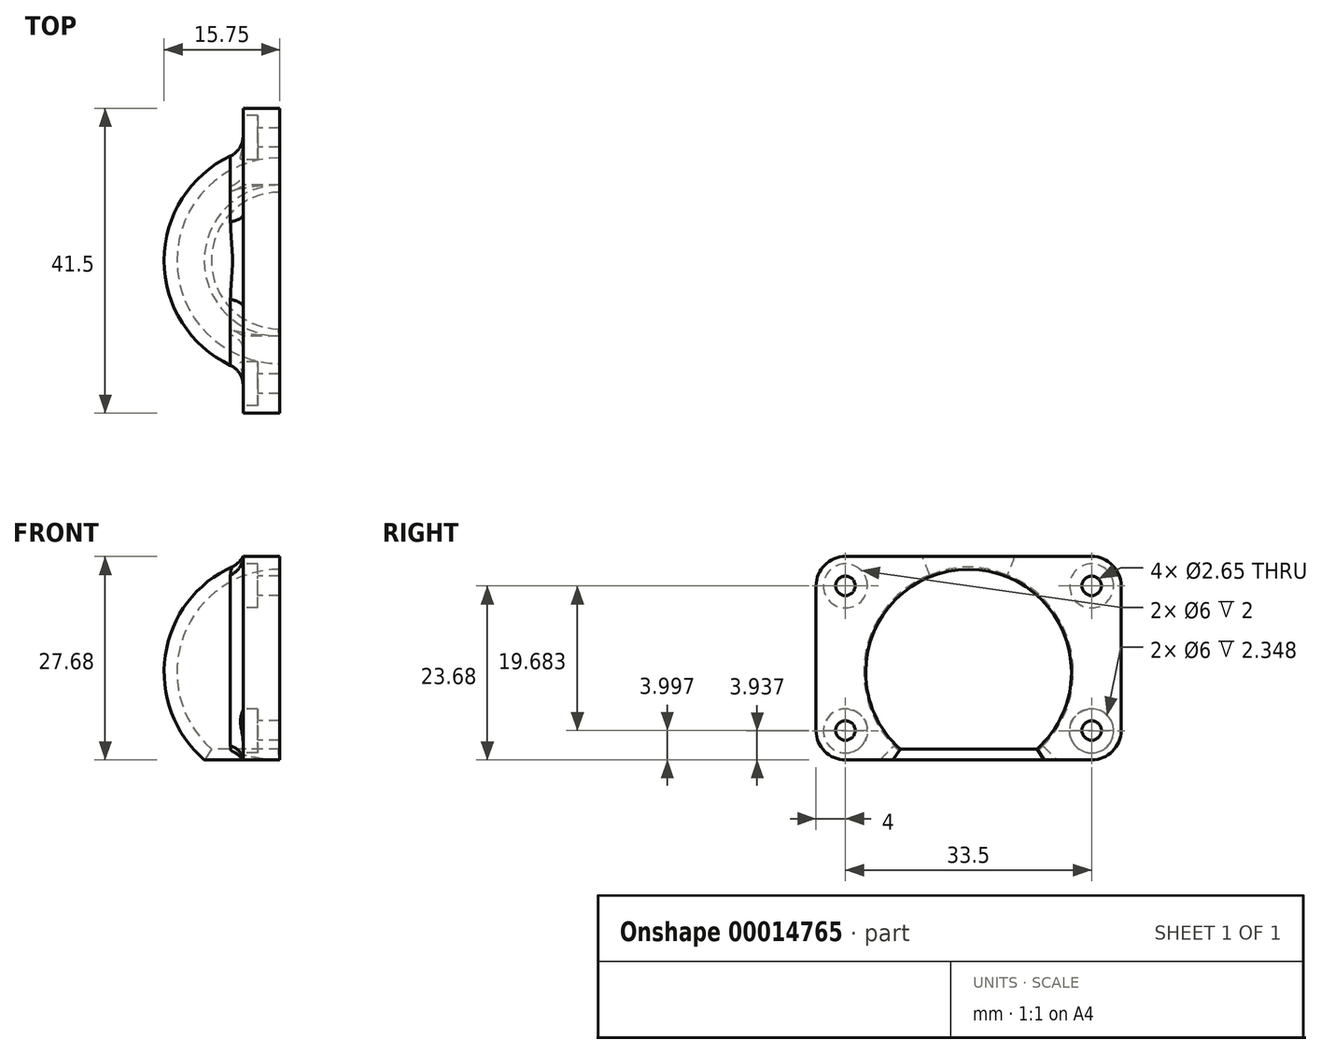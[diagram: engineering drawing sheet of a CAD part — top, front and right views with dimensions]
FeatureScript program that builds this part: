
annotation { "Feature Type Name" : "Feature", "Feature Type Description" : "" }
export const myFeature = defineFeature(function(context is Context, id is Id, definition is map)
    precondition{}
    {
        {
            var Q0;
            Q0=qCreatedBy(makeId("Top.planeOp"),FACE);
            var sketch = newSketch(context, id + "F0", { "sketchPlane" : qUnion([Q0])});
            skArc(sketch, "E0", {"start": v(0, 14) * mm, "mid": v(-14, 0) * mm, "end": v(0, -14) * mm});
            skArc(sketch, "E1", {"start": v(0, 15.75) * mm, "mid": v(-15.75, 0) * mm, "end": v(0, -15.75) * mm});
            skLineSegment(sketch, "E2", {"start": v(0, 14) * mm, "end": v(0, 15.75) * mm});
            skLineSegment(sketch, "E3", {"start": v(0, -14) * mm, "end": v(0, -15.75) * mm});
            skSolve(sketch);
        }
        {
            var Q0;
            Q0=makeQuery(id+"F0.imprint","IMPRINT",FACE,{"disambiguationData":[TD([[makeQuery(id+"F0.imprint","IMPRINT",EDGE,{"derivedFrom":sQuery(id+"F0.wireOp",EDGE,"E0")}),-1.0]])]});
            var Q1;
            Q1=sQuery(id+"F0.wireOp",EDGE,"E2");
            revolve(context, id + "F1", {"entities" : qUnion([Q0]), "axis" : qUnion([Q1]), "revolveType" : RevolveType.SYMMETRIC, "angle" : 180 * degree});
        }
        {
            var Q0;
            Q0=qCreatedBy(makeId("Top.planeOp"),FACE);
            var sketch = newSketch(context, id + "F2", { "sketchPlane" : qUnion([Q0])});
            skCircle(sketch, "E4", {"center": v(0, 0) * mm, "radius": 7.5 * mm});
            skSolve(sketch);
        }
        {
            var Q0;
            Q0=makeQuery(id+"F2.imprint","IMPRINT",FACE,{"disambiguationData":[TD([[makeQuery(id+"F2.imprint","IMPRINT",EDGE,{"derivedFrom":sQuery(id+"F2.wireOp",EDGE,"E4")}),1.0]])]});
            extrude(context, id + "F3", {"entities" : qUnion([Q0]), "operationType" : NewBodyOperationType.REMOVE, "oppositeDirection" : true, "depth" : 25 * mm});
        }
        {
            var Q0;
            Q0=qCreatedBy(makeId("Right.planeOp"),FACE);
            var sketch = newSketch(context, id + "F4", { "sketchPlane" : qUnion([Q0])});
            skPoint(sketch, "E5", {"position": v(0, -2.5) * mm});
            skLineSegment(sketch, "E6", {"start": v(2.76, -0.55) * mm, "end": v(12.1, -14.7) * mm});
            skLineSegment(sketch, "E7", {"start": v(2.76, -0.55) * mm, "end": v(0, -0.55) * mm});
            skLineSegment(sketch, "E8", {"start": v(0, -0.55) * mm, "end": v(0, -14.7) * mm});
            skLineSegment(sketch, "E9", {"start": v(0, -14.7) * mm, "end": v(12.1, -14.7) * mm});
            skPoint(sketch, "E10.left.end.orphan", {"position": v(5.75, -2.5) * mm});
            skPoint(sketch, "E11.trimOffspring.end.orphan", {"position": v(-5.75, -2.5) * mm});
            skSolve(sketch);
        }
        {
            var Q0;
            Q0=makeQuery(id+"F4.imprint","IMPRINT",FACE,{"disambiguationData":[TD([[makeQuery(id+"F4.imprint","IMPRINT",EDGE,{"derivedFrom":sQuery(id+"F4.wireOp",EDGE,"E6")}),-1.0]])]});
            var Q1;
            Q1=sQuery(id+"F4.wireOp",EDGE,"E8");
            revolve(context, id + "F5", {"operationType" : NewBodyOperationType.REMOVE, "entities" : qUnion([Q0]), "axis" : qUnion([Q1]), "revolveType" : RevolveType.FULL, "oppositeDirection" : true});
        }
        {
            var Q0;
            Q0=qCreatedBy(makeId("Right.planeOp"),FACE);
            cPlane(context, id + "F6", {"entities" : qUnion([Q0]), "cplaneType" : CPlaneType.OFFSET, "offset" : 5 * mm, "oppositeDirection" : true, "width" : 150 * mm, "height" : 150 * mm});
        }
        {
            var Q0;
            Q0=qCreatedBy(id+"F6.planeOp",FACE);
            var sketch = newSketch(context, id + "F7", { "sketchPlane" : qUnion([Q0])});
            skLineSegment(sketch, "E12.bottom", {"start": v(16.75, 15.75) * mm, "end": v(-16.75, 15.75) * mm});
            skLineSegment(sketch, "E12.top", {"start": v(16.75, -11.93) * mm, "end": v(10.28, -11.93) * mm});
            skLineSegment(sketch, "E12.left", {"start": v(20.75, 11.75) * mm, "end": v(20.75, -7.93) * mm});
            skLineSegment(sketch, "E12.right", {"start": v(-20.75, 11.75) * mm, "end": v(-20.75, -7.93) * mm});
            skPoint(sketch, "E13.visualSharp", {"position": v(-20.75, 15.75) * mm});
            skArc(sketch, "E13.filletArc", {"start": v(-16.75, 15.75) * mm, "mid": v(-19.58, 14.58) * mm, "end": v(-20.75, 11.75) * mm});
            skPoint(sketch, "E14.visualSharp", {"position": v(-20.75, -11.93) * mm});
            skArc(sketch, "E14.filletArc", {"start": v(-20.75, -7.93) * mm, "mid": v(-19.58, -10.76) * mm, "end": v(-16.75, -11.93) * mm});
            skPoint(sketch, "E15.visualSharp", {"position": v(20.75, -11.93) * mm});
            skArc(sketch, "E15.filletArc", {"start": v(16.75, -11.93) * mm, "mid": v(19.58, -10.76) * mm, "end": v(20.75, -7.93) * mm});
            skPoint(sketch, "E16.visualSharp", {"position": v(20.75, 15.75) * mm});
            skArc(sketch, "E16.filletArc", {"start": v(20.75, 11.75) * mm, "mid": v(19.58, 14.58) * mm, "end": v(16.75, 15.75) * mm});
            skArc(sketch, "E17", {"start": v(9.3, -10.46) * mm, "mid": v(0, 14) * mm, "end": v(-9.3, -10.46) * mm});
            skLineSegment(sketch, "E18", {"start": v(-9.3, -10.46) * mm, "end": v(-10.28, -11.93) * mm});
            skLineSegment(sketch, "E19", {"start": v(9.3, -10.46) * mm, "end": v(10.28, -11.93) * mm});
            skLineSegment(sketch, "E20.trimOffspring", {"start": v(-10.28, -11.93) * mm, "end": v(-16.75, -11.93) * mm});
            skSolve(sketch);
        }
        {
            var Q0;
            Q0=makeQuery(id+"F7.imprint","IMPRINT",FACE,{"disambiguationData":[TD([[makeQuery(id+"F7.imprint","IMPRINT",EDGE,{"derivedFrom":sQuery(id+"F7.wireOp",EDGE,"E12.bottom")}),1.0]])]});
            extrude(context, id + "F8", {"entities" : qUnion([Q0]), "operationType" : NewBodyOperationType.ADD, "depth" : 5 * mm});
        }
        {
            var Q0;
            Q0=makeQuery(id+"F8.boolean.opBoolean","INTERSECT",EDGE,{"derivedFrom":[makeQuery(id+"F1.opRevolve","SWEPT_FACE",FACE,{"disambiguationData":[OSD([sQuery(id+"F0.wireOp",EDGE,"E1")])]}),makeQuery(id+"F8.opExtrude","CAP_FACE",FACE,{"disambiguationData":[OSD([sQuery(id+"F7.wireOp",EDGE,"E12.bottom"),sQuery(id+"F7.wireOp",EDGE,"E12.top"),sQuery(id+"F7.wireOp",EDGE,"E12.left"),sQuery(id+"F7.wireOp",EDGE,"E12.right"),sQuery(id+"F7.wireOp",EDGE,"E13.filletArc"),sQuery(id+"F7.wireOp",EDGE,"E14.filletArc"),sQuery(id+"F7.wireOp",EDGE,"E15.filletArc"),sQuery(id+"F7.wireOp",EDGE,"E16.filletArc"),sQuery(id+"F7.wireOp",EDGE,"E17"),sQuery(id+"F7.wireOp",EDGE,"E18"),sQuery(id+"F7.wireOp",EDGE,"E19"),sQuery(id+"F7.wireOp",EDGE,"E20.trimOffspring")])],"isStart":true})]});
            fillet(context, id + "F9", {"entities" : qUnion([Q0]), "radius" : 3 * mm, "tangentPropagation" : true, "allowEdgeOverflow" : false});
        }
        {
            var Q0;
            Q0=makeQuery(id+"F8.boolean.opBoolean","MERGE",FACE,{"derivedFrom":[makeQuery(id+"F1.opRevolve","CAP_FACE",FACE,{"disambiguationData":[OSD([sQuery(id+"F0.wireOp",EDGE,"E0"),sQuery(id+"F0.wireOp",EDGE,"E1"),sQuery(id+"F0.wireOp",EDGE,"E2"),sQuery(id+"F0.wireOp",EDGE,"E3")])],"isStart":true}),makeQuery(id+"F8.opExtrude","CAP_FACE",FACE,{"disambiguationData":[OSD([sQuery(id+"F7.wireOp",EDGE,"E12.bottom"),sQuery(id+"F7.wireOp",EDGE,"E12.top"),sQuery(id+"F7.wireOp",EDGE,"E12.left"),sQuery(id+"F7.wireOp",EDGE,"E12.right"),sQuery(id+"F7.wireOp",EDGE,"E13.filletArc"),sQuery(id+"F7.wireOp",EDGE,"E14.filletArc"),sQuery(id+"F7.wireOp",EDGE,"E15.filletArc"),sQuery(id+"F7.wireOp",EDGE,"E16.filletArc"),sQuery(id+"F7.wireOp",EDGE,"E17"),sQuery(id+"F7.wireOp",EDGE,"E18"),sQuery(id+"F7.wireOp",EDGE,"E19"),sQuery(id+"F7.wireOp",EDGE,"E20.trimOffspring")])],"isStart":false})]});
            var sketch = newSketch(context, id + "F10", { "sketchPlane" : qUnion([Q0])});
            skPoint(sketch, "E21", {"position": v(-16.75, 11.75) * mm});
            skPoint(sketch, "E22", {"position": v(-16.75, -7.93) * mm});
            skPoint(sketch, "E23", {"position": v(16.75, -7.93) * mm});
            skPoint(sketch, "E24", {"position": v(16.75, 11.75) * mm});
            skSolve(sketch);
        }
        {
            var Q0;
            Q0=sQuery(id+"F10.wireOp",VERTEX,"E21");
            var Q1;
            Q1=sQuery(id+"F10.wireOp",VERTEX,"E22");
            var Q2;
            Q2=sQuery(id+"F10.wireOp",VERTEX,"E23");
            var Q3;
            Q3=sQuery(id+"F10.wireOp",VERTEX,"E24");
            var Q4;
            Q4=makeQuery(id+"F1.opRevolve","SWEPT_BODY",BODY,{"disambiguationData":[OSD([sQuery(id+"F0.wireOp",EDGE,"E0"),sQuery(id+"F0.wireOp",EDGE,"E1"),sQuery(id+"F0.wireOp",EDGE,"E2"),sQuery(id+"F0.wireOp",EDGE,"E3")])]});
            hole(context, id + "F11", {"style" : HoleStyle.SIMPLE, "endStyle" : HoleEndStyle.BLIND, "holeDiameter" : 2.65 * mm, "holeDepth" : 6 * mm, "locations" : qUnion([Q0, Q1, Q2, Q3]), "scope" : qUnion([Q4]), "startStyle" : HoleStartStyle.SKETCH});
        }
        {
            var Q0;
            Q0=qCreatedBy(id+"F6.planeOp",FACE);
            cPlane(context, id + "F12", {"entities" : qUnion([Q0]), "cplaneType" : CPlaneType.OFFSET, "offset" : 2 * mm, "oppositeDirection" : true, "width" : 150 * mm, "height" : 150 * mm});
        }
        {
            var Q0;
            Q0=qCreatedBy(id+"F12.planeOp",FACE);
            var sketch = newSketch(context, id + "F13", { "sketchPlane" : qUnion([Q0])});
            skCircle(sketch, "E25", {"center": v(16.75, 11.75) * mm, "radius": 3 * mm});
            skCircle(sketch, "E26", {"center": v(16.75, -8) * mm, "radius": 3 * mm});
            skCircle(sketch, "E27", {"center": v(-16.75, -8) * mm, "radius": 3 * mm});
            skCircle(sketch, "E28", {"center": v(-16.75, 11.75) * mm, "radius": 3 * mm});
            skSolve(sketch);
        }
        {
            var Q0;
            Q0=makeQuery(id+"F13.imprint","IMPRINT",FACE,{"disambiguationData":[TD([[makeQuery(id+"F13.imprint","IMPRINT",EDGE,{"derivedFrom":sQuery(id+"F13.wireOp",EDGE,"E25")}),1.0]])]});
            var Q1;
            Q1=makeQuery(id+"F13.imprint","IMPRINT",FACE,{"disambiguationData":[TD([[makeQuery(id+"F13.imprint","IMPRINT",EDGE,{"derivedFrom":sQuery(id+"F13.wireOp",EDGE,"E26")}),1.0]])]});
            var Q2;
            Q2=makeQuery(id+"F13.imprint","IMPRINT",FACE,{"disambiguationData":[TD([[makeQuery(id+"F13.imprint","IMPRINT",EDGE,{"derivedFrom":sQuery(id+"F13.wireOp",EDGE,"E27")}),1.0]])]});
            var Q3;
            Q3=makeQuery(id+"F13.imprint","IMPRINT",FACE,{"disambiguationData":[TD([[makeQuery(id+"F13.imprint","IMPRINT",EDGE,{"derivedFrom":sQuery(id+"F13.wireOp",EDGE,"E28")}),1.0]])]});
            extrude(context, id + "F14", {"entities" : qUnion([Q0, Q1, Q2, Q3]), "operationType" : NewBodyOperationType.REMOVE, "depth" : 4 * mm});
        }
    });
